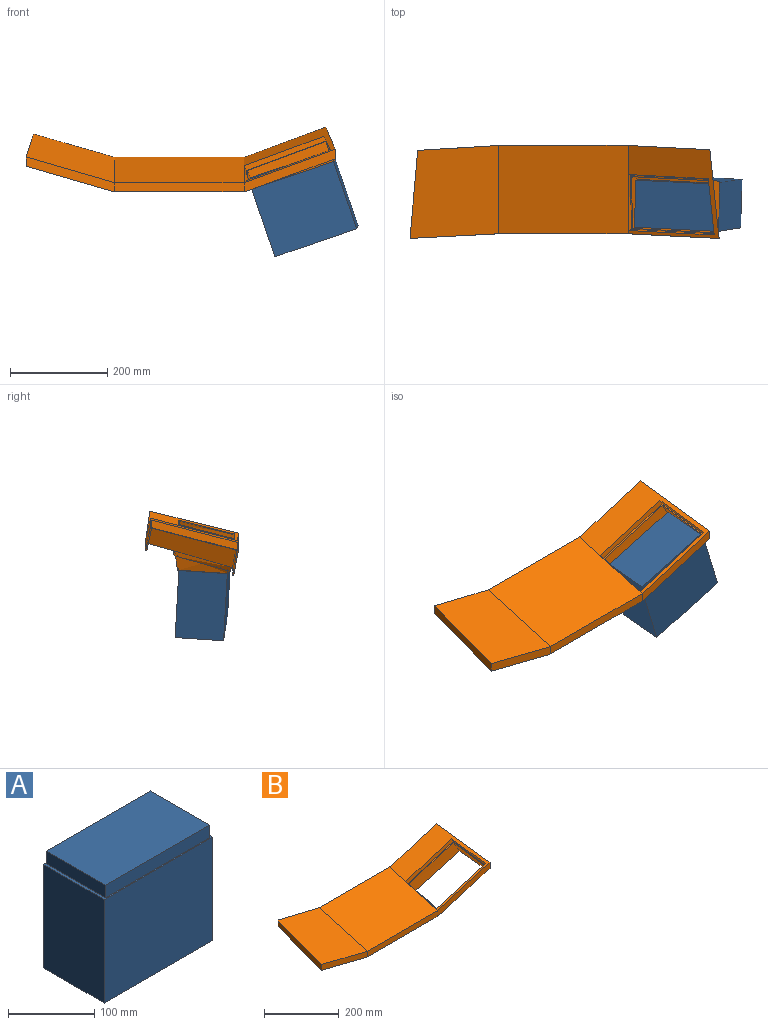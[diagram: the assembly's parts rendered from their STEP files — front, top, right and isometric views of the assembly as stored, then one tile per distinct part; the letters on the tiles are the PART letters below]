
ASSEMBLY  parts=2 mates=1
PART A: 11 faces, bbox 178x100x165 mm
  f0: plane 147x100mm, normal (1,0,0), area 14700mm2, adj f1,f3,f4,f9
  f1: plane 178x147mm, normal (0,1,0), area 26166mm2, adj f0,f2,f4,f9
  f2: plane 147x100mm, normal (-1,0,0), area 14700mm2, adj f1,f3,f4,f9
  f3: plane 178x147mm, normal (0,-1,0), area 26166mm2, adj f0,f2,f4,f9
  f4: plane 178x100mm, normal (0,0,-1), area 17800mm2, adj f0,f1,f2,f3
  f5: plane 171x18mm, normal (0,1,0), area 3078mm2, adj f6,f8,f9,f10
  f6: plane 97x18mm, normal (1,0,0), area 1746mm2, adj f5,f7,f9,f10
  f7: plane 171x18mm, normal (0,-1,0), area 3078mm2, adj f6,f8,f9,f10
  f8: plane 97x18mm, normal (-1,0,0), area 1746mm2, adj f5,f7,f9,f10
  f9: plane 178x100mm, normal (0,0,1), area 1213mm2, adj f0,f1,f2,f3,f5,f6,f7,f8
  f10: plane 171x97mm, normal (0,0,1), area 16587mm2, adj f5,f6,f7,f8
PART B: 45 faces, bbox 651.3x201.6x142.8 mm
  f0: plane 272.43x2.71mm, normal (0,0.28,-0.96), area 719.9mm2, adj f2,f4,f9,f12,f13,f16,f21,f24
  f1: plane 272.43x2.71mm, normal (0,0.28,-0.96), area 719.9mm2, adj f2,f3,f7,f11,f12,f15,f19,f23
  f2: plane 191x179.62mm, normal (-0.28,0.26,-0.92), area 1433.5mm2, adj f0,f1,f6,f7,f9,f18,f19,f21
  f3: plane 266.7x18.5mm, normal (0,-1,0), area 4933mm2, adj f1,f5,f7,f11
  f4: plane 266.7x18.5mm, normal (0,1,0), area 4933mm2, adj f0,f5,f9,f13
  f5: plane 266.7x181.61mm, normal (0,-0.28,0.96), area 50387.3mm2, adj f3,f4,f8,f14
  f6: plane 180.98x66.33mm, normal (-1,0.09,0), area 3502.5mm2, adj f2,f7,f8,f9
  f7: plane 182.18x71.49mm, normal (0.05,-1,0), area 3515.9mm2, adj f1,f2,f3,f6,f8
  f8: plane 191.16x182.18mm, normal (0.28,-0.26,0.92), area 34171mm2, adj f5,f6,f7,f9
  f9: plane 166.34x66.48mm, normal (-0.06,1,0), area 3211.9mm2, adj f0,f2,f4,f6,f8
  f10: plane 182.62x64.71mm, normal (0.99,0.1,0), area 3620.2mm2, adj f11,f12,f13,f14
  f11: plane 187.33x87.64mm, normal (-0.05,-1,0), area 3696.5mm2, adj f1,f3,f10,f12,f14
  f12: plane 191.26x184.16mm, normal (0.35,0.26,-0.9), area 1369.3mm2, adj f0,f1,f10,f11,f13,f22,f23,f24
  f13: plane 168.14x80.56mm, normal (0.05,1,0), area 3317.6mm2, adj f0,f4,f10,f12,f14
  f14: plane 192.08x187.98mm, normal (-0.35,-0.26,0.9), area 14040.9mm2, adj f5,f10,f11,f13,f31,f32,f33,f34
  f15: plane 266.83x15.85mm, normal (0,1,0), area 4230.4mm2, adj f1,f17,f19,f23
  f16: plane 266.56x15.85mm, normal (0,-1,0), area 4226mm2, adj f0,f17,f21,f24
  f17: plane 268.12x177.15mm, normal (0,0.28,-0.96), area 48965.8mm2, adj f15,f16,f19,f20,f21,f23,f24,f25
  f18: plane 175.89x62.26mm, normal (1,-0.09,0), area 2917.7mm2, adj f2,f19,f20,f21
  f19: plane 179.32x67.93mm, normal (-0.05,1,0), area 2966.4mm2, adj f1,f2,f15,f17,f18,f20
  f20: plane 185.9x179.03mm, normal (-0.28,0.26,-0.92), area 32653.4mm2, adj f17,f18,f19,f21
  f21: plane 164.08x63.05mm, normal (0.06,-1,0), area 2715.4mm2, adj f0,f2,f16,f17,f18,f20
  f22: plane 177.5x60.64mm, normal (-0.99,-0.1,0), area 2455.1mm2, adj f12,f23,f24,f25,f27,f28,f29,f37
  f23: plane 184.43x83.78mm, normal (0.05,1,0), area 3119.1mm2, adj f1,f12,f15,f17,f22,f25
  f24: plane 165.91x76.9mm, normal (-0.05,-1,0), area 2805.5mm2, adj f0,f12,f16,f17,f22,f25
  f25: plane 186.23x184.1mm, normal (0.35,0.26,-0.9), area 11165.8mm2, adj f17,f22,f23,f24,f28,f29,f30
  f26: offset ~132.99x64.47mm, area 1336.8mm2, adj f17,f27,f28,f30
  f27: plane 181.49x125.92mm, normal (0.35,0.26,-0.9), area 1434.9mm2, adj f22,f26,f28,f29,f30,f36,f37,f38
  f28: offset ~205.69x117.67mm, area 1989.7mm2, adj f17,f22,f25,f26,f27,f29
  f29: offset ~133.22x63.43mm, area 966.4mm2, adj f22,f25,f27,f28,f30
  f30: offset ~202.91x95.06mm, area 1961.5mm2, adj f17,f25,f26,f27,f29
  f31: offset ~126.13x65.06mm, area 1233.8mm2, adj f14,f32,f34,f40
  f32: offset ~198.49x114.44mm, area 1935.6mm2, adj f14,f31,f33,f40
  f33: offset ~126.43x64.47mm, area 1212.2mm2, adj f14,f32,f34,f40
  f34: offset ~196.72x92.96mm, area 1913.9mm2, adj f14,f31,f33,f40
  f35: plane 176.02x114.36mm, normal (0.33,0.05,-0.94), area 1450.8mm2, adj f36,f37,f38,f39,f41,f42,f43,f44
  f36: offset ~192.64x88.14mm, area 1824.9mm2, adj f27,f35,f37,f39
  f37: offset ~122.98x57.58mm, area 2377.1mm2, adj f12,f22,f27,f35,f36,f38
  f38: offset ~195.53x110.05mm, area 6196mm2, adj f12,f22,f27,f35,f37,f39
  f39: offset ~122.43x56.89mm, area 2112.5mm2, adj f27,f35,f36,f38
  f40: plane 176.49x121.31mm, normal (-0.35,-0.26,0.9), area 1524.4mm2, adj f31,f32,f33,f34,f41,f42,f43,f44
  f41: bspline ~187.56x83.06mm, area 2330.2mm2, adj f35,f40,f42,f44
  f42: bspline ~114.24x51.86mm, area 2774.6mm2, adj f35,f40,f41,f43
  f43: bspline ~186.46x102.43mm, area 6398.9mm2, adj f35,f40,f42,f44
  f44: bspline ~116.9x50.02mm, area 2324.4mm2, adj f35,f40,f41,f43
PLACE A rot(axis=(0.18,-0.98,-0.11),19.4deg) t=(228.6,-31.04,53.78)mm
PLACE B at identity fixed
MATE fastened A.f9 <-> B.f35  axis (-0.33,-0.05,0.94) through (233.03,-79.98,33.53)mm
